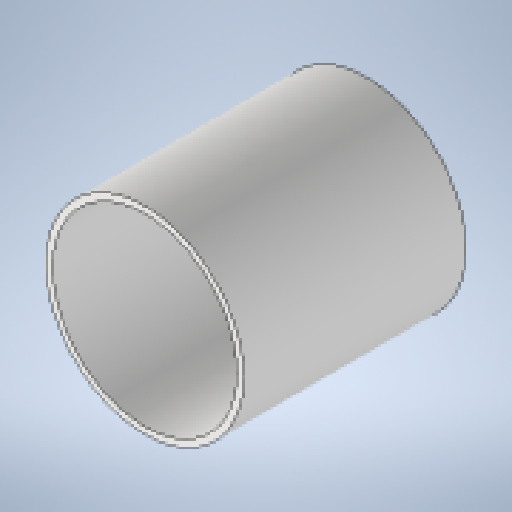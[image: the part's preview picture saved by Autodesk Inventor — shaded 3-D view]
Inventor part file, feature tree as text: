
AUTODESK INVENTOR PART (.ipt)
format: ipt  version: 2025.1 (Build 291241020, 241B)  size: 155,648 bytes
history: native  units: mm
features: extrude x1, sketch x1
ambient origin geometry x8: Origin, YZ Plane, XZ Plane, XY Plane, X Axis, Y Axis, Z Axis, Center Point
bodies: Solid1 (feature_tree)
feature tree (2):
  extrude  "Extrusion1"  Depth=100.0mm
  sketch  "Sketch1"  dims[d0=89.0mm d1=3.0mm d2=100.0mm d3=0.0mm]
